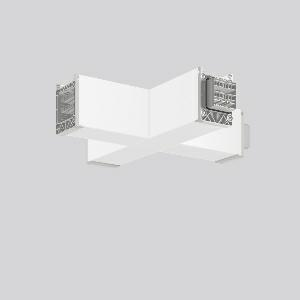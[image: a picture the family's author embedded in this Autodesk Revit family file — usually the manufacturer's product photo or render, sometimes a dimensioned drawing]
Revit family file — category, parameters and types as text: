
# Revit family: linedo_x-verbindung_982775_002_1_4e16
name_source: partatom
category: Lighting Fixtures
units: mm (PartAtom-declared; Revit-internal decimal feet)

## family parameters
Cut with Voids When Loaded = No
Host = Face
Light Source = No
Part Type = Normal
Room Calculation Point = No
Round Connector Dimension = Use Diameter
Shared = No

## types (1)
- LINEDO X-Verbindung
    Apparent Load = 0 VA
    Default Elevation = 1800 mm
    Description = Series: LINEDO
X-connector, 7-pole, connection plug / socket / plug / socket. Housing: extruded aluminium profile, powder-coated. Cover made of plastic, surface like housing. LINEDO plug system, plastic, light grey. Easy connection for rigid or flexible wires. 6 membrane cable entries (2 x M20 and 4 x M25). Suitable for power supply in 7-pole version. Ready prewired. Colour-coded individual cables enable easy electromechanical separation.
Colour: traffic white, matt (RAL 9016)
Length: 330 mm
Width: 330 mm
Height: 76 mm
Weight: 1230 g
    Height = 76 mm
    Lamp = 0 x
    Length = 331 mm
    Luminous efficacy = 0 lm/W
    Manufacturer = RZB
    ModVariant = No
    Model = 982775.002.1
    Mounting Place = Ceiling
    Mounting Type = Surface mounted
    Number of Poles = 1
    OnlyDefault = Yes
    Power Factor = 1
    Product Name = LINEDO X-Verbindung
    Product group = Surface mounted continuous line luminaire system
    ProductGroupID = 310
    Protection Class = Protection class I
    Protection Degree = Degree of protection
    RLX_Detail_Level = 1
    RLX_Emergency_Light_Flux = 0 lm
    RLX_Emergency_Type = 0
    RLX_Emergency_Type_DB = No
    RlxData = <blob elided: 18357 chars, md5=b6994596>
    Standby Power = 0 W
    System Light Flux = 0 lm
    System Power = 0 W
    Type Comments = Product without accessories
    Type Image = 982775.002.jpg
    URL = http://relux.com
    VarID = ---
    Voltage = 0 V
    Weight = 0.00 kg
    Width = 331 mm

## geometry (parser evidence)
native form markers: Blend x4, Sweep x13
no freeform markers — native parametric forms only
